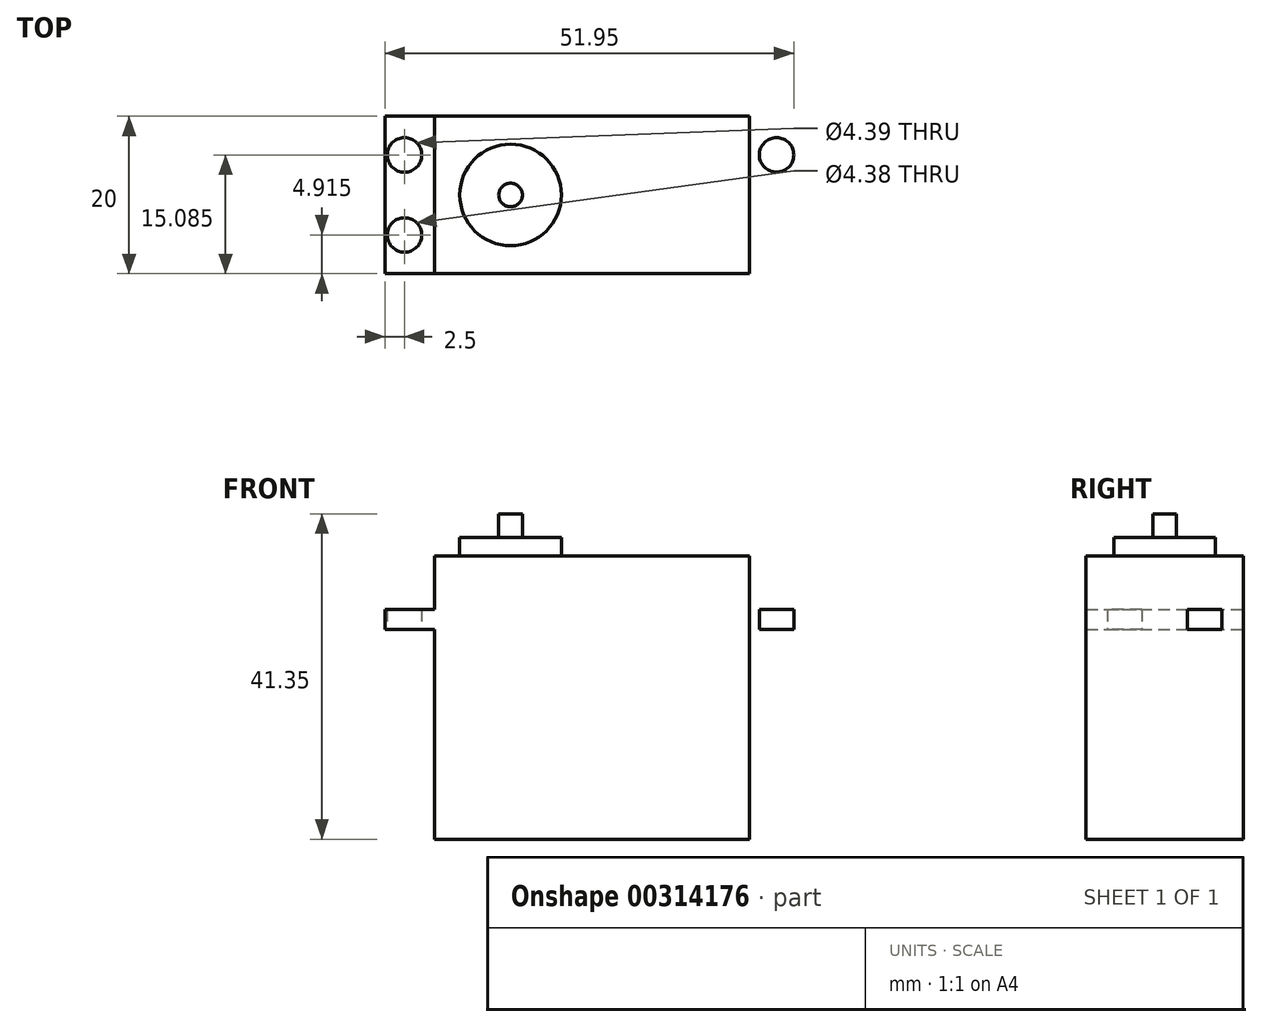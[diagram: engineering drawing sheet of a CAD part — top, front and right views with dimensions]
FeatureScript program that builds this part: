
annotation { "Feature Type Name" : "Feature", "Feature Type Description" : "" }
export const myFeature = defineFeature(function(context is Context, id is Id, definition is map)
    precondition{}
    {
        {
            var Q0;
            Q0=qCreatedBy(makeId("Front.planeOp"),FACE);
            var sketch = newSketch(context, id + "F0", { "sketchPlane" : qUnion([Q0])});
            skLineSegment(sketch, "E0.bottom", {"start": v(-9.66, 9.35) * mm, "end": v(30.32, 9.35) * mm});
            skLineSegment(sketch, "E0.top", {"start": v(-9.66, -26.67) * mm, "end": v(30.32, -26.67) * mm});
            skLineSegment(sketch, "E0.left", {"start": v(-9.66, 9.35) * mm, "end": v(-9.66, -26.67) * mm});
            skLineSegment(sketch, "E0.right", {"start": v(30.32, 9.35) * mm, "end": v(30.32, -26.67) * mm});
            skLineSegment(sketch, "E1", {"start": v(0, 22.65) * mm, "end": v(0, -56.26) * mm, "construction": true});
            skLineSegment(sketch, "E2", {"start": v(-36.44, 0) * mm, "end": v(35.03, 0) * mm, "construction": true});
            skPoint(sketch, "E3", {"position": v(0, 0) * mm});
            skLineSegment(sketch, "E4.bottom", {"start": v(-9.66, 0) * mm, "end": v(-15.97, 0) * mm});
            skLineSegment(sketch, "E4.top", {"start": v(-9.66, 2.5) * mm, "end": v(-15.97, 2.5) * mm});
            skLineSegment(sketch, "E4.left", {"start": v(-9.66, 0) * mm, "end": v(-9.66, 2.5) * mm});
            skLineSegment(sketch, "E4.right", {"start": v(-15.97, 0) * mm, "end": v(-15.97, 2.5) * mm});
            skLineSegment(sketch, "E5.bottom", {"start": v(30.32, 0) * mm, "end": v(36.29, 0) * mm});
            skLineSegment(sketch, "E5.top", {"start": v(30.32, 2.5) * mm, "end": v(36.29, 2.5) * mm});
            skLineSegment(sketch, "E5.left", {"start": v(30.32, 0) * mm, "end": v(30.32, 2.5) * mm});
            skLineSegment(sketch, "E5.right", {"start": v(36.29, 0) * mm, "end": v(36.29, 2.5) * mm});
            skLineSegment(sketch, "E6", {"start": v(-13.47, 22.85) * mm, "end": v(-13.47, -47.39) * mm, "construction": true});
            skLineSegment(sketch, "E7", {"start": v(33.8, 23.26) * mm, "end": v(33.8, -47.39) * mm, "construction": true});
            skLineSegment(sketch, "E8.bottom", {"start": v(-6.45, 9.35) * mm, "end": v(6.45, 9.35) * mm});
            skLineSegment(sketch, "E8.top", {"start": v(0, 11.68) * mm, "end": v(6.45, 11.68) * mm});
            skLineSegment(sketch, "E8.right", {"start": v(6.45, 9.35) * mm, "end": v(6.45, 11.68) * mm});
            skPoint(sketch, "E9", {"position": v(0, 11.68) * mm});
            skLineSegment(sketch, "E10", {"start": v(0, 11.68) * mm, "end": v(0, 9.35) * mm});
            skLineSegment(sketch, "E11.left", {"start": v(0, 11.68) * mm, "end": v(0, 14.68) * mm});
            skSolve(sketch);
        }
        {
            var Q0;
            {var subQ4=sQuery(id+"F0.wireOp",EDGE,"E0.top");Q0=makeQuery(id+"F0.imprint","IMPRINT",FACE,{"disambiguationData":[TD([[makeQuery(id+"F0.imprint","IMPRINT",EDGE,{"derivedFrom":subQ4}),1.0]])]});}
            var Q1;
            Q1=makeQuery(id+"F0.imprint","IMPRINT",FACE,{"disambiguationData":[TD([[makeQuery(id+"F0.imprint","IMPRINT",EDGE,{"derivedFrom":sQuery(id+"F0.wireOp",EDGE,"E5.bottom")}),1.0]])]});
            var Q2;
            Q2=makeQuery(id+"F0.imprint","IMPRINT",FACE,{"disambiguationData":[TD([[makeQuery(id+"F0.imprint","IMPRINT",EDGE,{"derivedFrom":sQuery(id+"F0.wireOp",EDGE,"E4.bottom")}),-1.0]])]});
            extrude(context, id + "F1", {"entities" : qUnion([Q0, Q1, Q2]), "endBound" : BoundingType.SYMMETRIC, "depth" : 20 * mm});
        }
        {
            var Q0;
            Q0=makeQuery(id+"F0.imprint","IMPRINT",FACE,{"disambiguationData":[TD([[makeQuery(id+"F0.imprint","IMPRINT",EDGE,{"derivedFrom":sQuery(id+"F0.wireOp",EDGE,"E8.top")}),-1.0]])]});
            var Q1;
            Q1=sQuery(id+"F0.wireOp",EDGE,"E1");
            revolve(context, id + "F2", {"operationType" : NewBodyOperationType.ADD, "entities" : qUnion([Q0]), "axis" : qUnion([Q1]), "revolveType" : RevolveType.FULL});
        }
        {
            var Q0;
            Q0=makeQuery(id+"F1.opExtrude","SWEPT_FACE",FACE,{"disambiguationData":[OSD([sQuery(id+"F0.wireOp",EDGE,"E4.bottom")])]});
            var sketch = newSketch(context, id + "F3", { "sketchPlane" : qUnion([Q0])});
            skLineSegment(sketch, "E12", {"start": v(-13.47, 7.88) * mm, "end": v(-13.47, -7.48) * mm, "construction": true});
            skCircle(sketch, "E13", {"center": v(-13.47, 5.08) * mm, "radius": 2.19 * mm});
            skCircle(sketch, "E14", {"center": v(-13.47, -5.08) * mm, "radius": 2.2 * mm});
            skSolve(sketch);
        }
        {
            var Q0;
            Q0=makeQuery(id+"F3.imprint","IMPRINT",FACE,{"disambiguationData":[TD([[makeQuery(id+"F3.imprint","IMPRINT",EDGE,{"derivedFrom":sQuery(id+"F3.wireOp",EDGE,"E13")}),1.0]])]});
            var Q1;
            Q1=makeQuery(id+"F3.imprint","IMPRINT",FACE,{"disambiguationData":[TD([[makeQuery(id+"F3.imprint","IMPRINT",EDGE,{"derivedFrom":sQuery(id+"F3.wireOp",EDGE,"E14")}),1.0]])]});
            var Q2;
            Q2=makeQuery(id+"F1.opExtrude","SWEPT_FACE",FACE,{"disambiguationData":[OSD([sQuery(id+"F0.wireOp",EDGE,"E4.top")])]});
            extrude(context, id + "F4", {"entities" : qUnion([Q0, Q1]), "operationType" : NewBodyOperationType.REMOVE, "endBound" : BoundingType.UP_TO_SURFACE, "oppositeDirection" : true, "endBoundEntityFace" : qUnion([Q2]), "depth" : 25 * mm});
        }
        {
            var Q0;
            Q0=makeQuery(id+"F1.opExtrude","SWEPT_FACE",FACE,{"disambiguationData":[OSD([sQuery(id+"F0.wireOp",EDGE,"E5.bottom")])]});
            var sketch = newSketch(context, id + "F5", { "sketchPlane" : qUnion([Q0])});
            skLineSegment(sketch, "E15", {"start": v(33.8, 12.01) * mm, "end": v(33.8, -15.41) * mm, "construction": true});
            skCircle(sketch, "E16", {"center": v(33.8, 5.08) * mm, "radius": 2.19 * mm});
            skCircle(sketch, "E17.MirrorC", {"center": v(33.8, -5.08) * mm, "radius": 2.19 * mm});
            skSolve(sketch);
        }
        {
            var Q0;
            Q0=makeQuery(id+"F5.imprint","IMPRINT",FACE,{"disambiguationData":[TD([[makeQuery(id+"F5.imprint","IMPRINT",EDGE,{"derivedFrom":sQuery(id+"F5.wireOp",EDGE,"E16")}),1.0]])]});
            var Q1;
            Q1=makeQuery(id+"F5.imprint","IMPRINT",FACE,{"disambiguationData":[TD([[makeQuery(id+"F5.imprint","IMPRINT",EDGE,{"derivedFrom":sQuery(id+"F5.wireOp",EDGE,"E17.MirrorC")}),-1.0]])]});
            var Q2;
            Q2=makeQuery(id+"F1.opExtrude","SWEPT_FACE",FACE,{"disambiguationData":[OSD([sQuery(id+"F0.wireOp",EDGE,"E5.top")])]});
            extrude(context, id + "F6", {"entities" : qUnion([Q0, Q1]), "operationType" : NewBodyOperationType.REMOVE, "endBound" : BoundingType.UP_TO_SURFACE, "oppositeDirection" : true, "endBoundEntityFace" : qUnion([Q2]), "depth" : 25 * mm});
        }
        {
            var Q0;
            Q0=makeQuery(id+"F2.opRevolve","SWEPT_FACE",FACE,{"disambiguationData":[OSD([sQuery(id+"F0.wireOp",EDGE,"E8.top")])]});
            var sketch = newSketch(context, id + "F7", { "sketchPlane" : qUnion([Q0])});
            skCircle(sketch, "E18", {"center": v(0, 0) * mm, "radius": 1.5 * mm});
            skSolve(sketch);
        }
        {
            var Q0;
            Q0=makeQuery(id+"F7.imprint","IMPRINT",FACE,{"disambiguationData":[TD([[makeQuery(id+"F7.imprint","IMPRINT",EDGE,{"derivedFrom":sQuery(id+"F7.wireOp",EDGE,"E18")}),1.0]])]});
            extrude(context, id + "F8", {"entities" : qUnion([Q0]), "operationType" : NewBodyOperationType.ADD, "depth" : 3 * mm});
        }
    });
